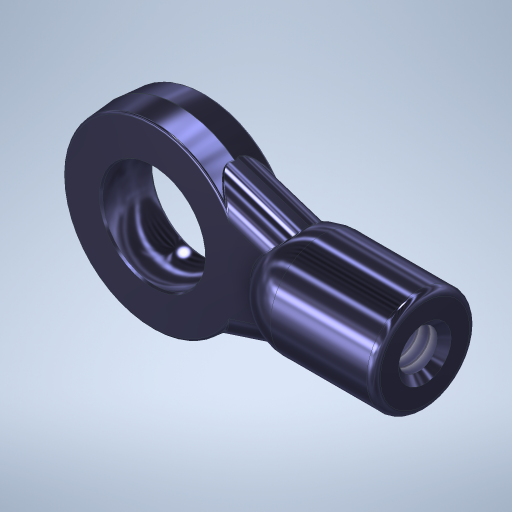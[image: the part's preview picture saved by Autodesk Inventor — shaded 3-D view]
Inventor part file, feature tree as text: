
AUTODESK INVENTOR PART (.ipt)
format: ipt  version: 2023.1 (Build 271208000, 208)  size: 521,216 bytes
history: native  units: in
note: dims shown in document units (in); Inventor stores cm internally (conversion verified against a paired STEP export)
features: sketch x5, fillet x4, extrude x2, revolve x2, draft x2, chamfer x2, projected_geometry x2, split x1, hole x1
ambient origin geometry x8: Origin, YZ Plane, XZ Plane, XY Plane, X Axis, Y Axis, Z Axis, Center Point
bodies: Solid1 (feature_tree)
feature tree (21):
  extrude  "Extrusion1"  Depth=0.115in TaperAngle=0.0deg
  revolve  "Revolution1"  [1 undecoded]
  extrude  "Extrusion2"  Depth=0.1375in
  fillet  "Fillet1"  Radius=0.3961in
  split  "Split1"
  draft  "FaceDraft1"
  draft  "FaceDraft2"
  hole  "Hole1"  [1 undecoded]
  fillet  "Fillet2"  Radius=0.05in
  fillet  "Fillet3"  Radius=0.0344in
  fillet  "Fillet4"  Radius=0.0344in
  chamfer  "Chamfer1"  Distance=0.015in
  revolve  "Revolution2"  [1 undecoded]
  chamfer  "Chamfer2"  Distance=0.005in
  sketch  "Sketch1"  dims[d0=0.4in d1=0.115in d2=0.0in]
  sketch  "Sketch2"  dims[d3=0.225in d4=0.225in]
  sketch  "Sketch3"  dims[d5=90.0deg d6=0.1375in d7=0.3961in]
  sketch  "Sketch4"  dims[d8=0.3154in d9=0.115in d10=0.0in d11=0.05in d12=0.0344in d13=0.0344in]
  sketch  "Sketch5"  dims[d14=0.0849in d15=0.224in d16=0.375in d17=0.25in d18=0.5635in d19=0.225in d20=0.8108in d21=0.015in d22=0.005in d23=0.005in d24=0.015in d25=0.125in d26=45.0deg d27=0.125in d28=90.0deg d29=0.005in d30=0.125in d31=45.0deg]
  projected_geometry  "Project Cut Edges1"
  projected_geometry  "Project Cut Edges2"
note: 3 required parameter values undecoded (feature->parameter linkage not recoverable at this tier; creation-order binding heuristic only, values carry confidence <= 0.55)